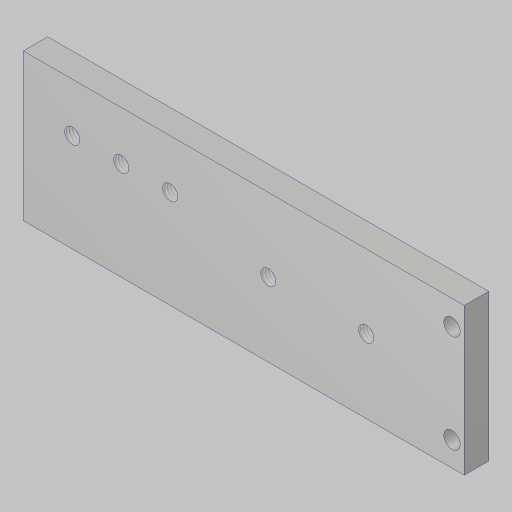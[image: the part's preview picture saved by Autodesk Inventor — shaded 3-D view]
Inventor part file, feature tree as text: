
AUTODESK INVENTOR PART (.ipt)
format: ipt  version: 2023.5 (Build 275446000, 446)  size: 133,120 bytes
history: native  units: in
note: dims shown in document units (in); Inventor stores cm internally (conversion verified against a paired STEP export)
features: sketch x4, hole x3, extrude x1
ambient origin geometry x8: Origin, YZ Plane, XZ Plane, XY Plane, X Axis, Y Axis, Z Axis, Center Point
bodies: Solid1 (feature_tree)
feature tree (8):
  extrude  "Extrusion1"  Depth=1.5in
  hole  "Hole1"  [1 undecoded]
  hole  "Hole2"  [1 undecoded]
  hole  "Hole3"  [1 undecoded]
  sketch  "Sketch1"  dims[d0=4.5in d1=1.5in]
  sketch  "Sketch2"  dims[d2=0.25in d3=0.0in d4=0.5in d5=0.5in]
  sketch  "Sketch3"  dims[d6=0.5in]
  sketch  "Sketch5"  dims[d7=0.156in d8=0.38in d9=0.385in d10=0.25in d11=0.5635in d12=1.0in d13=0.8108in d14=0.5in d15=0.5in d16=0.25in d17=0.25in d18=0.125in d19=0.17in d20=0.328in d21=0.332in d22=0.25in d23=0.5635in d24=1.0in d25=0.8108in d28=1.0in d30=0.156in d31=0.38in d32=0.375in d33=0.25in d34=0.5635in d35=1.0in d36=0.8108in d37=1.5in]
note: 3 required parameter values undecoded (feature->parameter linkage not recoverable at this tier; creation-order binding heuristic only, values carry confidence <= 0.55)
